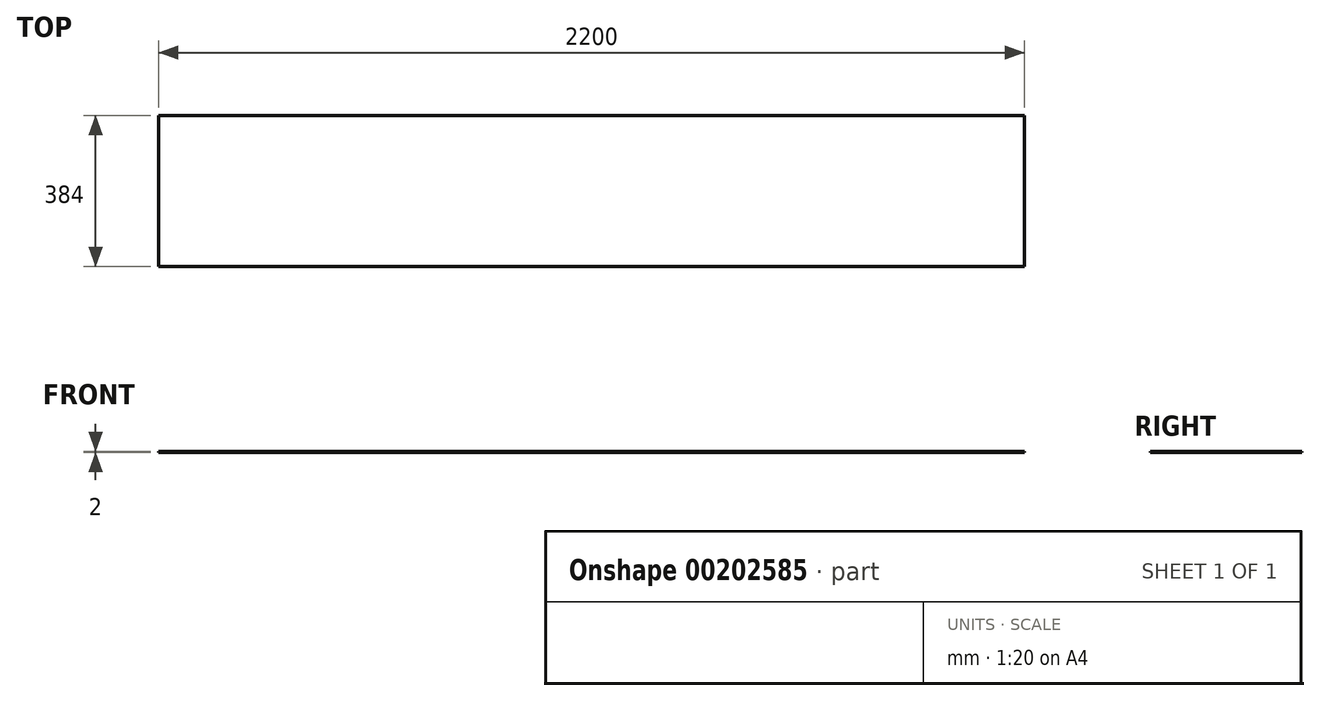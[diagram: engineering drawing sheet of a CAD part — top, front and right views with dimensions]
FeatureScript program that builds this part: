
annotation { "Feature Type Name" : "Feature", "Feature Type Description" : "" }
export const myFeature = defineFeature(function(context is Context, id is Id, definition is map)
    precondition{}
    {
        {
            var Q0;
            Q0=qCreatedBy(makeId("Top.planeOp"),FACE);
            var sketch = newSketch(context, id + "F0", { "sketchPlane" : qUnion([Q0])});
            skLineSegment(sketch, "E0.bottom", {"start": v(-864.34, -235.28) * mm, "end": v(1335.66, -235.28) * mm});
            skLineSegment(sketch, "E0.top", {"start": v(-864.34, 148.72) * mm, "end": v(1335.66, 148.72) * mm});
            skLineSegment(sketch, "E0.left", {"start": v(-864.34, -235.28) * mm, "end": v(-864.34, 148.72) * mm});
            skLineSegment(sketch, "E0.right", {"start": v(1335.66, -235.28) * mm, "end": v(1335.66, 148.72) * mm});
            skSolve(sketch);
        }
        {
            var Q0;
            Q0=makeQuery(id+"F0.imprint","IMPRINT",FACE,{"disambiguationData":[TD([[makeQuery(id+"F0.imprint","IMPRINT",EDGE,{"derivedFrom":sQuery(id+"F0.wireOp",EDGE,"E0.bottom")}),1.0]])]});
            extrude(context, id + "F1", {"entities" : qUnion([Q0]), "depth" : 2 * mm});
        }
    });
